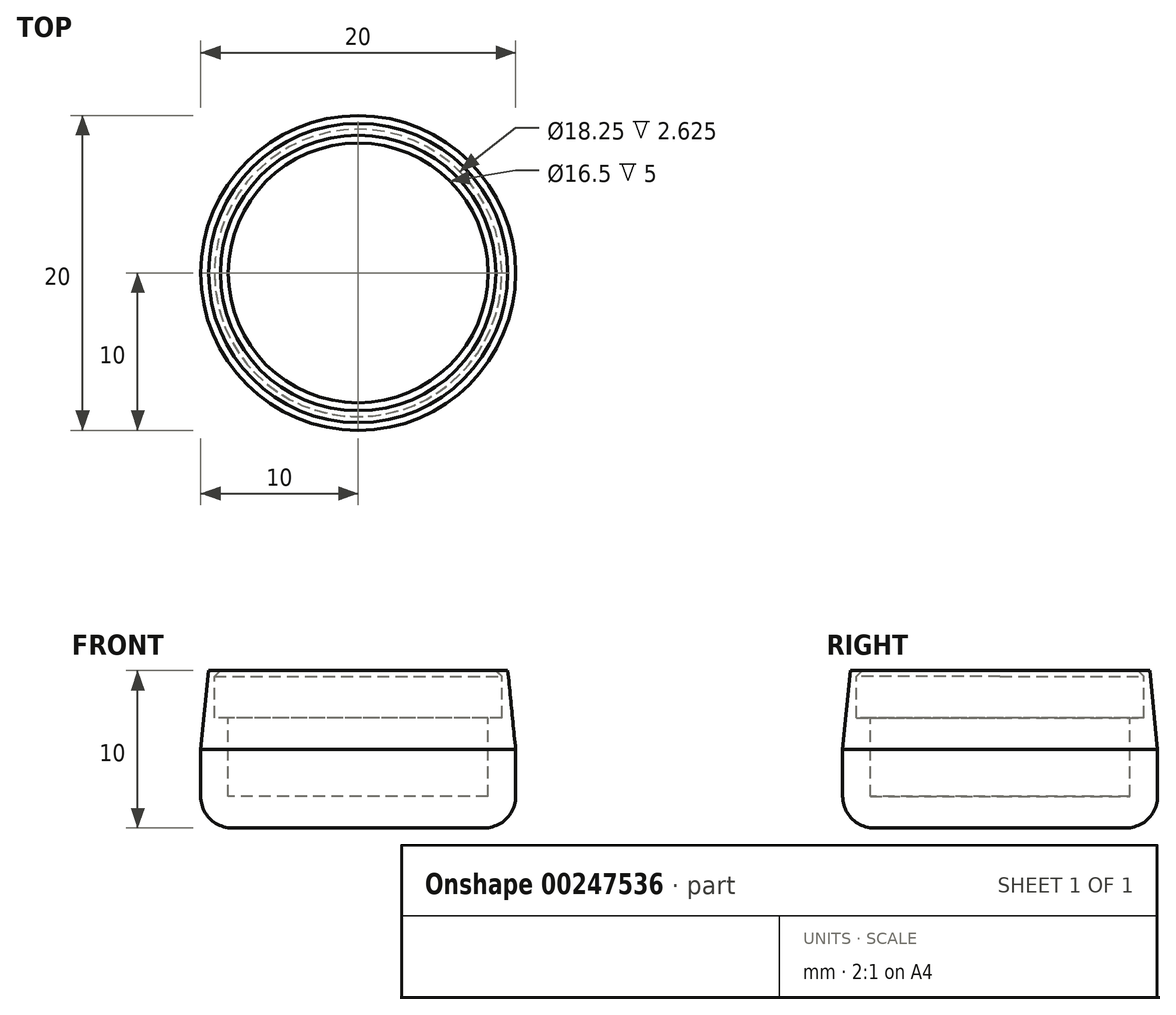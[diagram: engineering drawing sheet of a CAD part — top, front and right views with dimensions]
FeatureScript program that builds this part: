
annotation { "Feature Type Name" : "Feature", "Feature Type Description" : "" }
export const myFeature = defineFeature(function(context is Context, id is Id, definition is map)
    precondition{}
    {
        {
            var Q0;
            Q0=qCreatedBy(makeId("Top.planeOp"),FACE);
            var sketch = newSketch(context, id + "F0", { "sketchPlane" : qUnion([Q0])});
            skCircle(sketch, "E0", {"center": v(0, 0) * mm, "radius": 10 * mm});
            skSolve(sketch);
        }
        {
            var Q0;
            Q0=makeQuery(id+"F0.imprint","IMPRINT",FACE,{"disambiguationData":[TD([[makeQuery(id+"F0.imprint","IMPRINT",EDGE,{"derivedFrom":sQuery(id+"F0.wireOp",EDGE,"E0")}),1.0]])]});
            extrude(context, id + "F1", {"entities" : qUnion([Q0]), "depth" : 10 * mm});
        }
        {
            var Q0;
            Q0=makeQuery(id+"F1.opExtrude","CAP_FACE",FACE,{"disambiguationData":[OSD([sQuery(id+"F0.wireOp",EDGE,"E0")])],"isStart":false});
            var sketch = newSketch(context, id + "F2", { "sketchPlane" : qUnion([Q0])});
            skCircle(sketch, "E1", {"center": v(0, 0) * mm, "radius": 8.25 * mm});
            skSolve(sketch);
        }
        {
            var Q0;
            Q0=makeQuery(id+"F2.imprint","IMPRINT",FACE,{"disambiguationData":[TD([[makeQuery(id+"F2.imprint","IMPRINT",EDGE,{"derivedFrom":sQuery(id+"F2.wireOp",EDGE,"E1")}),1.0]])]});
            extrude(context, id + "F3", {"entities" : qUnion([Q0]), "operationType" : NewBodyOperationType.REMOVE, "oppositeDirection" : true, "depth" : 8 * mm});
        }
        {
            var Q0;
            Q0=makeQuery(id+"F1.opExtrude","CAP_FACE",FACE,{"disambiguationData":[OSD([sQuery(id+"F0.wireOp",EDGE,"E0")])],"isStart":false});
            var sketch = newSketch(context, id + "F4", { "sketchPlane" : qUnion([Q0])});
            skCircle(sketch, "E2", {"center": v(0, 0) * mm, "radius": 9.12 * mm});
            skSolve(sketch);
        }
        {
            var Q0;
            Q0=makeQuery(id+"F4.imprint","IMPRINT",FACE,{"disambiguationData":[TD([[makeQuery(id+"F4.imprint","IMPRINT",EDGE,{"derivedFrom":sQuery(id+"F4.wireOp",EDGE,"E2")}),1.0]])]});
            extrude(context, id + "F5", {"entities" : qUnion([Q0]), "operationType" : NewBodyOperationType.REMOVE, "oppositeDirection" : true, "depth" : 3 * mm});
        }
        {
            var Q0;
            Q0=makeQuery(id+"F1.opExtrude","CAP_FACE",FACE,{"disambiguationData":[OSD([sQuery(id+"F0.wireOp",EDGE,"E0")])],"isStart":false});
            var sketch = newSketch(context, id + "F6", { "sketchPlane" : qUnion([Q0])});
            skCircle(sketch, "E3", {"center": v(0, 0) * mm, "radius": 8.75 * mm});
            skCircle(sketch, "E4", {"center": v(0, 0) * mm, "radius": 9.12 * mm});
            skSolve(sketch);
        }
        {
            var Q0;
            Q0=makeQuery(id+"F6.imprint","IMPRINT",FACE,{"disambiguationData":[TD([[makeQuery(id+"F6.imprint","IMPRINT",EDGE,{"derivedFrom":sQuery(id+"F6.wireOp",EDGE,"E3")}),-1.0]])]});
            extrude(context, id + "F7", {"entities" : qUnion([Q0]), "operationType" : NewBodyOperationType.ADD, "oppositeDirection" : true, "depth" : 1 * mm});
        }
        {
            var Q0;
            Q0=makeQuery(id+"F1.opExtrude","CAP_EDGE",EDGE,{"disambiguationData":[OSD([sQuery(id+"F0.wireOp",EDGE,"E0")])],"isStart":true});
            fillet(context, id + "F8", {"entities" : qUnion([Q0]), "radius" : 2 * mm, "tangentPropagation" : true, "allowEdgeOverflow" : false});
        }
        {
            var Q0;
            Q0=makeQuery(id+"F7.opExtrude","CAP_EDGE",EDGE,{"disambiguationData":[OSD([sQuery(id+"F6.wireOp",EDGE,"E3")])],"isStart":false});
            chamfer(context, id + "F9", {"entities" : qUnion([Q0]), "width" : 1 * mm, "tangentPropagation" : true});
        }
        {
            var Q0;
            Q0=makeQuery(id+"F1.opExtrude","CAP_EDGE",EDGE,{"disambiguationData":[OSD([sQuery(id+"F0.wireOp",EDGE,"E0")])],"isStart":false});
            chamfer(context, id + "F10", {"entities" : qUnion([Q0]), "chamferType" : ChamferType.TWO_OFFSETS, "width1" : .5 * mm, "oppositeDirection" : false, "width2" : 5 * mm, "tangentPropagation" : true});
        }
    });
